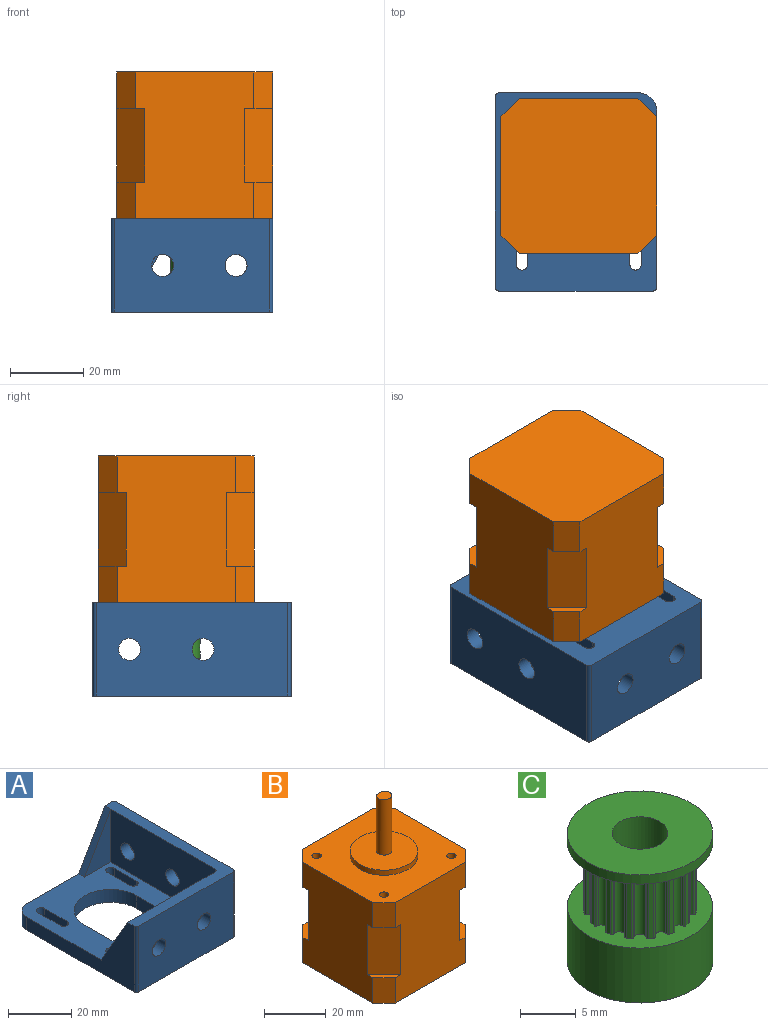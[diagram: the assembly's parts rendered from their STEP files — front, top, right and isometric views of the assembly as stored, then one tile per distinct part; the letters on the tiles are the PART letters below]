
ASSEMBLY  parts=3 mates=4
PART A: 42 faces, bbox 44x54x25.4 mm
  f0: plane 50x40mm, normal (0,0,1), area 1136mm2, adj f1,f2,f3,f4,f5,f6,f7,f8
  f1: cylinder r=1.55mm len=5mm, axis (0,0,-1), area 24.3mm2, adj f0,f2,f24,f25
  f2: plane 10x5mm, normal (-1,0,0), area 50mm2, adj f0,f1,f3,f25
  f3: cylinder r=1.55mm len=5mm, axis (0,0,-1), area 24.3mm2, adj f0,f2,f24,f25
  f4: plane 10x5mm, normal (-1,0,0), area 50mm2, adj f0,f5,f19,f25
  f5: cylinder r=1.55mm len=5mm, axis (0,0,-1), area 24.3mm2, adj f0,f4,f6,f25
  f6: plane 10x5mm, normal (1,0,0), area 50mm2, adj f0,f5,f19,f25
  f7: cylinder r=11.5mm len=23mm, axis (0,0,-1), area 180.6mm2, adj f0,f8,f20,f25
  f8: plane 10x5mm, normal (-1,0,0), area 50mm2, adj f0,f7,f9,f25
  f9: cylinder r=11.5mm len=23mm, axis (0,0,-1), area 180.6mm2, adj f0,f8,f20,f25
  f10: cylinder r=1.55mm len=5mm, axis (0,0,-1), area 24.3mm2, adj f0,f11,f21,f25
  f11: plane 10x5mm, normal (-1,0,0), area 50mm2, adj f0,f10,f12,f25
  f12: cylinder r=1.55mm len=5mm, axis (0,0,-1), area 24.3mm2, adj f0,f11,f21,f25
  f13: cylinder r=1.55mm len=5mm, axis (0,0,-1), area 24.3mm2, adj f0,f14,f22,f25
  f14: plane 10x5mm, normal (-1,0,0), area 50mm2, adj f0,f13,f15,f25
  f15: cylinder r=1.55mm len=5mm, axis (0,0,-1), area 24.3mm2, adj f0,f14,f22,f25
  f16: plane 38x25.4mm, normal (0,1,0), area 371mm2, adj f0,f25,f30,f38,f39,f40
  f17: plane 48x25.4mm, normal (-1,0,0), area 421.1mm2, adj f0,f25,f30,f36,f39,f41
  f18: plane 42x25.4mm, normal (0,-1,0), area 1010.3mm2, adj f25,f30,f31,f32,f36,f37
  f19: cylinder r=1.55mm len=5mm, axis (0,0,-1), area 24.3mm2, adj f0,f4,f6,f25
  f20: plane 10x5mm, normal (1,0,0), area 50mm2, adj f0,f7,f9,f25
  f21: plane 10x5mm, normal (1,0,0), area 50mm2, adj f0,f10,f12,f25
  f22: plane 10x5mm, normal (1,0,0), area 50mm2, adj f0,f13,f15,f25
  f23: plane 52x25.4mm, normal (1,0,0), area 1264.3mm2, adj f25,f30,f33,f34,f37,f38
  f24: plane 10x5mm, normal (1,0,0), area 50mm2, adj f0,f1,f3,f25
  f25: plane 54x44mm, normal (0,0,-1), area 1570.3mm2, adj f1,f2,f3,f4,f5,f6,f7,f8
  f26: plane 20.4x11.75mm, normal (0,-1,0), area 119.8mm2, adj f0,f27,f40
  f27: plane 46.5x20.4mm, normal (-1,0,0), area 892.1mm2, adj f0,f26,f30,f33,f34,f35
  f28: plane 36.5x20.4mm, normal (0,1,0), area 688.1mm2, adj f0,f29,f30,f31,f32,f35
  f29: plane 20.4x11.75mm, normal (1,0,0), area 119.9mm2, adj f0,f28,f41
  f30: plane 54x44mm, normal (0,0,1), area 375.6mm2, adj f16,f17,f18,f23,f27,f28,f35,f36
  f31: cylinder r=3mm len=6mm, axis (0,1,0), area 75.4mm2, adj f18,f28
  f32: cylinder r=3mm len=6mm, axis (0,1,0), area 75.4mm2, adj f18,f28
  f33: cylinder r=3mm len=6mm, axis (-1,0,0), area 75.4mm2, adj f23,f27
  f34: cylinder r=3mm len=6mm, axis (-1,0,0), area 75.4mm2, adj f23,f27
  f35: cylinder r=1mm len=20.4mm, axis (0,0,1), area 32mm2, adj f0,f27,f28,f30
  f36: cylinder r=1mm len=25.4mm, axis (0,0,-1), area 39.9mm2, adj f17,f18,f25,f30
  f37: cylinder r=1mm len=25.4mm, axis (0,0,-1), area 39.9mm2, adj f18,f23,f25,f30
  f38: cylinder r=1mm len=25.4mm, axis (0,0,1), area 39.9mm2, adj f16,f23,f25,f30
  f39: cylinder r=5mm len=5mm, axis (0,0,1), area 39.3mm2, adj f0,f16,f17,f25
  f40: plane 20.4x11.75mm, normal (-0.87,0,0.5), area 58.9mm2, adj f0,f16,f26,f30
  f41: plane 20.4x11.75mm, normal (0,0.87,0.5), area 58.9mm2, adj f0,f17,f29,f30
PART B: 40 faces, bbox 42.4x42.4x64 mm
  f0: plane 40x32.26mm, normal (-1,0,0), area 1188.7mm2, adj f5,f6,f10,f11,f12,f14,f15,f18
  f1: plane 40x32.26mm, normal (0,-1,0), area 1188.7mm2, adj f4,f5,f8,f11,f12,f13,f14,f17
  f2: plane 40x32.26mm, normal (1,0,0), area 1188.7mm2, adj f4,f7,f8,f9,f12,f13,f16,f17
  f3: plane 40x32.26mm, normal (0,1,0), area 1188.7mm2, adj f6,f7,f9,f10,f12,f15,f16,f19
  f4: plane 20x7.62mm, normal (0.71,-0.71,0), area 215.5mm2, adj f1,f2,f8,f17
  f5: plane 20x7.62mm, normal (-0.71,-0.71,0), area 215.5mm2, adj f0,f1,f11,f18
  f6: plane 20x7.62mm, normal (-0.71,0.71,0), area 215.5mm2, adj f0,f3,f10,f19
  f7: plane 20x7.62mm, normal (0.71,0.71,0), area 215.5mm2, adj f2,f3,f9,f20
  f8: plane 7.62x7.62mm, normal (0,0,-1), area 16.1mm2, adj f1,f2,f4,f13
  f9: plane 7.62x7.62mm, normal (0,0,-1), area 16.1mm2, adj f2,f3,f7,f16
  f10: plane 7.62x7.62mm, normal (0,0,-1), area 16.1mm2, adj f0,f3,f6,f15
  f11: plane 7.62x7.62mm, normal (0,0,-1), area 16.1mm2, adj f0,f1,f5,f14
  f12: plane 42.42x42.42mm, normal (0,0,1), area 1339.4mm2, adj f0,f1,f2,f3,f13,f14,f15,f16
  f13: plane 10x5.08mm, normal (0.71,-0.71,0), area 71.8mm2, adj f1,f2,f8,f12
  f14: plane 10x5.08mm, normal (-0.71,-0.71,0), area 71.8mm2, adj f0,f1,f11,f12
  f15: plane 10x5.08mm, normal (-0.71,0.71,0), area 71.8mm2, adj f0,f3,f10,f12
  f16: plane 10x5.08mm, normal (0.71,0.71,0), area 71.8mm2, adj f2,f3,f9,f12
  f17: plane 7.62x7.62mm, normal (0,0,1), area 16.1mm2, adj f1,f2,f4,f23
  f18: plane 7.62x7.62mm, normal (0,0,1), area 16.1mm2, adj f0,f1,f5,f24
  f19: plane 7.62x7.62mm, normal (0,0,1), area 16.1mm2, adj f0,f3,f6,f21
  f20: plane 7.62x7.62mm, normal (0,0,1), area 16.1mm2, adj f2,f3,f7,f22
  f21: plane 10x5.08mm, normal (-0.71,0.71,0), area 71.8mm2, adj f0,f3,f19,f25
  f22: plane 10x5.08mm, normal (0.71,0.71,0), area 71.8mm2, adj f2,f3,f20,f25
  f23: plane 10x5.08mm, normal (0.71,-0.71,0), area 71.8mm2, adj f1,f2,f17,f25
  f24: plane 10x5.08mm, normal (-0.71,-0.71,0), area 71.8mm2, adj f0,f1,f18,f25
  f25: plane 42.42x42.42mm, normal (0,0,-1), area 1747.7mm2, adj f0,f1,f2,f3,f21,f22,f23,f24
  f26: cylinder r=11mm len=22mm, axis (0,0,-1), area 138.2mm2, adj f12,f27
  f27: plane 22x22mm, normal (0,0,1), area 360.4mm2, adj f26,f28
  f28: cylinder r=2.5mm len=22mm, axis (0,0,-1), area 297.3mm2, adj f27,f29,f30,f31
  f29: plane 5x4.5mm, normal (0,0,1), area 18.6mm2, adj f28,f31
  f30: plane 3x0.5mm, normal (0,0,1), area 1mm2, adj f28,f31
  f31: plane 15x3mm, normal (0,1,0), area 45mm2, adj f28,f29,f30
  f32: cylinder r=1.5mm len=6.35mm, axis (0,0,1), area 59.8mm2, adj f12,f33
  f33: plane 3x3mm, normal (0,0,1), area 7.1mm2, adj f32
  f34: cylinder r=1.5mm len=6.35mm, axis (0,0,1), area 59.8mm2, adj f12,f35
  f35: plane 3x3mm, normal (0,0,1), area 7.1mm2, adj f34
  f36: cylinder r=1.5mm len=6.35mm, axis (0,0,1), area 59.8mm2, adj f12,f37
  f37: plane 3x3mm, normal (0,0,1), area 7.1mm2, adj f36
  f38: cylinder r=1.5mm len=6.35mm, axis (0,0,1), area 59.8mm2, adj f12,f39
  f39: plane 3x3mm, normal (0,0,1), area 7.1mm2, adj f38
PART C: 104 faces, bbox 13x13x14 mm
  f0: cylinder r=2.5mm len=14mm, axis (0,0,1), area 214.8mm2, adj f2,f102,f103
  f1: cylinder r=6.5mm len=13mm, axis (0,0,1), area 240.1mm2, adj f2,f3,f103
  f2: plane 13x13mm, normal (0,0,-1), area 113.1mm2, adj f0,f1
  f3: plane 13x13mm, normal (0,0,1), area 62.7mm2, adj f1,f4,f5,f6,f7,f8,f9,f10
  f4: cylinder r=0.15mm len=7mm, axis (0,0,-1), area 1.7mm2, adj f3,f5,f99,f100
  f5: cylinder r=1mm len=7mm, axis (0,0,-1), area 1.7mm2, adj f3,f4,f6,f100
  f6: cylinder r=0.56mm len=7mm, axis (0,0,-1), area 9mm2, adj f3,f5,f7,f100
  f7: cylinder r=1mm len=7mm, axis (0,0,-1), area 1.7mm2, adj f3,f6,f8,f100
  f8: cylinder r=0.15mm len=7mm, axis (0,0,-1), area 1.7mm2, adj f3,f7,f9,f100
  f9: plane 7x0.49mm, normal (0.98,0.2,0), area 3.5mm2, adj f3,f8,f10,f100
  f10: cylinder r=0.15mm len=7mm, axis (0,0,-1), area 1.7mm2, adj f3,f9,f11,f100
  f11: cylinder r=1mm len=7mm, axis (0,0,-1), area 1.7mm2, adj f3,f10,f12,f100
  f12: cylinder r=0.56mm len=7mm, axis (0,0,-1), area 9mm2, adj f3,f11,f13,f100
  f13: cylinder r=1mm len=7mm, axis (0,0,-1), area 1.7mm2, adj f3,f12,f14,f100
  f14: cylinder r=0.15mm len=7mm, axis (0,0,-1), area 1.7mm2, adj f3,f13,f15,f100
  f15: plane 7x0.41mm, normal (0.83,0.56,0), area 3.5mm2, adj f3,f14,f16,f100
  f16: cylinder r=0.15mm len=7mm, axis (0,0,-1), area 1.7mm2, adj f3,f15,f17,f100
  f17: cylinder r=1mm len=7mm, axis (0,0,-1), area 1.7mm2, adj f3,f16,f18,f100
  f18: cylinder r=0.56mm len=7mm, axis (0,0,-1), area 9mm2, adj f3,f17,f19,f100
  f19: cylinder r=1mm len=7mm, axis (0,0,-1), area 1.7mm2, adj f3,f18,f20,f100
  f20: cylinder r=0.15mm len=7mm, axis (0,0,-1), area 1.7mm2, adj f3,f19,f21,f100
  f21: plane 7x0.41mm, normal (0.56,0.83,0), area 3.5mm2, adj f3,f20,f22,f100
  f22: cylinder r=0.15mm len=7mm, axis (0,0,-1), area 1.7mm2, adj f3,f21,f23,f100
  f23: cylinder r=1mm len=7mm, axis (0,0,-1), area 1.7mm2, adj f3,f22,f24,f100
  f24: cylinder r=0.56mm len=7mm, axis (0,0,-1), area 9mm2, adj f3,f23,f25,f100
  f25: cylinder r=1mm len=7mm, axis (0,0,-1), area 1.7mm2, adj f3,f24,f26,f100
  f26: cylinder r=0.15mm len=7mm, axis (0,0,-1), area 1.7mm2, adj f3,f25,f27,f100
  f27: plane 7x0.49mm, normal (0.2,0.98,0), area 3.5mm2, adj f3,f26,f28,f100
  f28: cylinder r=0.15mm len=7mm, axis (0,0,-1), area 1.7mm2, adj f3,f27,f29,f100
  f29: cylinder r=1mm len=7mm, axis (0,0,-1), area 1.7mm2, adj f3,f28,f30,f100
  f30: cylinder r=0.56mm len=7mm, axis (0,0,-1), area 9mm2, adj f3,f29,f31,f100
  f31: cylinder r=1mm len=7mm, axis (0,0,-1), area 1.7mm2, adj f3,f30,f32,f100
  f32: cylinder r=0.15mm len=7mm, axis (0,0,-1), area 1.7mm2, adj f3,f31,f33,f100
  f33: plane 7x0.49mm, normal (-0.2,0.98,0), area 3.5mm2, adj f3,f32,f34,f100
  f34: cylinder r=0.15mm len=7mm, axis (0,0,-1), area 1.7mm2, adj f3,f33,f35,f100
  f35: cylinder r=1mm len=7mm, axis (0,0,-1), area 1.7mm2, adj f3,f34,f36,f100
  f36: cylinder r=0.56mm len=7mm, axis (0,0,-1), area 9mm2, adj f3,f35,f37,f100
  f37: cylinder r=1mm len=7mm, axis (0,0,-1), area 1.7mm2, adj f3,f36,f38,f100
  f38: cylinder r=0.15mm len=7mm, axis (0,0,-1), area 1.7mm2, adj f3,f37,f39,f100
  f39: plane 7x0.41mm, normal (-0.56,0.83,0), area 3.5mm2, adj f3,f38,f40,f100
  f40: cylinder r=0.15mm len=7mm, axis (0,0,-1), area 1.7mm2, adj f3,f39,f41,f100
  f41: cylinder r=1mm len=7mm, axis (0,0,-1), area 1.7mm2, adj f3,f40,f42,f100
  f42: cylinder r=0.56mm len=7mm, axis (0,0,-1), area 9mm2, adj f3,f41,f43,f100
  f43: cylinder r=1mm len=7mm, axis (0,0,-1), area 1.7mm2, adj f3,f42,f44,f100
  f44: cylinder r=0.15mm len=7mm, axis (0,0,-1), area 1.7mm2, adj f3,f43,f45,f100
  f45: plane 7x0.41mm, normal (-0.83,0.56,0), area 3.5mm2, adj f3,f44,f46,f100
  f46: cylinder r=0.15mm len=7mm, axis (0,0,-1), area 1.7mm2, adj f3,f45,f47,f100
  f47: cylinder r=1mm len=7mm, axis (0,0,-1), area 1.7mm2, adj f3,f46,f48,f100
  f48: cylinder r=0.56mm len=7mm, axis (0,0,-1), area 9mm2, adj f3,f47,f49,f100
  f49: cylinder r=1mm len=7mm, axis (0,0,-1), area 1.7mm2, adj f3,f48,f50,f100
  f50: cylinder r=0.15mm len=7mm, axis (0,0,-1), area 1.7mm2, adj f3,f49,f51,f100
  f51: plane 7x0.49mm, normal (-0.98,0.2,0), area 3.5mm2, adj f3,f50,f52,f100
  f52: cylinder r=0.15mm len=7mm, axis (0,0,-1), area 1.7mm2, adj f3,f51,f53,f100
  f53: cylinder r=1mm len=7mm, axis (0,0,-1), area 1.7mm2, adj f3,f52,f54,f100
  f54: cylinder r=0.56mm len=7mm, axis (0,0,-1), area 9mm2, adj f3,f53,f55,f100
  f55: cylinder r=1mm len=7mm, axis (0,0,-1), area 1.7mm2, adj f3,f54,f56,f100
  f56: cylinder r=0.15mm len=7mm, axis (0,0,-1), area 1.7mm2, adj f3,f55,f57,f100
  f57: plane 7x0.49mm, normal (-0.98,-0.2,0), area 3.5mm2, adj f3,f56,f58,f100
  f58: cylinder r=0.15mm len=7mm, axis (0,0,-1), area 1.7mm2, adj f3,f57,f59,f100
  f59: cylinder r=1mm len=7mm, axis (0,0,-1), area 1.7mm2, adj f3,f58,f60,f100
  f60: cylinder r=0.56mm len=7mm, axis (0,0,-1), area 9mm2, adj f3,f59,f61,f100
  f61: cylinder r=1mm len=7mm, axis (0,0,-1), area 1.7mm2, adj f3,f60,f62,f100
  f62: cylinder r=0.15mm len=7mm, axis (0,0,-1), area 1.7mm2, adj f3,f61,f63,f100
  f63: plane 7x0.41mm, normal (-0.83,-0.56,0), area 3.5mm2, adj f3,f62,f64,f100
  f64: cylinder r=0.15mm len=7mm, axis (0,0,-1), area 1.7mm2, adj f3,f63,f65,f100
  f65: cylinder r=1mm len=7mm, axis (0,0,-1), area 1.7mm2, adj f3,f64,f66,f100
  f66: cylinder r=0.56mm len=7mm, axis (0,0,-1), area 9mm2, adj f3,f65,f67,f100
  f67: cylinder r=1mm len=7mm, axis (0,0,-1), area 1.7mm2, adj f3,f66,f68,f100
  f68: cylinder r=0.15mm len=7mm, axis (0,0,-1), area 1.7mm2, adj f3,f67,f69,f100
  f69: plane 7x0.41mm, normal (-0.56,-0.83,0), area 3.5mm2, adj f3,f68,f70,f100
  f70: cylinder r=0.15mm len=7mm, axis (0,0,-1), area 1.7mm2, adj f3,f69,f71,f100
  f71: cylinder r=1mm len=7mm, axis (0,0,-1), area 1.7mm2, adj f3,f70,f72,f100
  f72: cylinder r=0.56mm len=7mm, axis (0,0,-1), area 9mm2, adj f3,f71,f73,f100
  f73: cylinder r=1mm len=7mm, axis (0,0,-1), area 1.7mm2, adj f3,f72,f74,f100
  f74: cylinder r=0.15mm len=7mm, axis (0,0,-1), area 1.7mm2, adj f3,f73,f75,f100
  f75: plane 7x0.49mm, normal (-0.2,-0.98,0), area 3.5mm2, adj f3,f74,f76,f100
  f76: cylinder r=0.15mm len=7mm, axis (0,0,-1), area 1.7mm2, adj f3,f75,f77,f100
  f77: cylinder r=1mm len=7mm, axis (0,0,-1), area 1.7mm2, adj f3,f76,f78,f100
  f78: cylinder r=0.56mm len=7mm, axis (0,0,-1), area 9mm2, adj f3,f77,f79,f100
  f79: cylinder r=1mm len=7mm, axis (0,0,-1), area 1.7mm2, adj f3,f78,f80,f100
  f80: cylinder r=0.15mm len=7mm, axis (0,0,-1), area 1.7mm2, adj f3,f79,f81,f100
  f81: plane 7x0.49mm, normal (0.2,-0.98,0), area 3.5mm2, adj f3,f80,f82,f100
  f82: cylinder r=0.15mm len=7mm, axis (0,0,-1), area 1.7mm2, adj f3,f81,f83,f100
  f83: cylinder r=1mm len=7mm, axis (0,0,-1), area 1.7mm2, adj f3,f82,f84,f100
  f84: cylinder r=0.56mm len=7mm, axis (0,0,-1), area 9mm2, adj f3,f83,f85,f100
  f85: cylinder r=1mm len=7mm, axis (0,0,-1), area 1.7mm2, adj f3,f84,f86,f100
  f86: cylinder r=0.15mm len=7mm, axis (0,0,-1), area 1.7mm2, adj f3,f85,f87,f100
  f87: plane 7x0.41mm, normal (0.56,-0.83,0), area 3.5mm2, adj f3,f86,f88,f100
  f88: cylinder r=0.15mm len=7mm, axis (0,0,-1), area 1.7mm2, adj f3,f87,f89,f100
  f89: cylinder r=1mm len=7mm, axis (0,0,-1), area 1.7mm2, adj f3,f88,f90,f100
  f90: cylinder r=0.56mm len=7mm, axis (0,0,-1), area 9mm2, adj f3,f89,f91,f100
  f91: cylinder r=1mm len=7mm, axis (0,0,-1), area 1.7mm2, adj f3,f90,f92,f100
  f92: cylinder r=0.15mm len=7mm, axis (0,0,-1), area 1.7mm2, adj f3,f91,f93,f100
  f93: plane 7x0.41mm, normal (0.83,-0.56,0), area 3.5mm2, adj f3,f92,f94,f100
  f94: cylinder r=0.15mm len=7mm, axis (0,0,-1), area 1.7mm2, adj f3,f93,f95,f100
  f95: cylinder r=1mm len=7mm, axis (0,0,-1), area 1.7mm2, adj f3,f94,f96,f100
  f96: cylinder r=0.56mm len=7mm, axis (0,0,-1), area 9mm2, adj f3,f95,f97,f100
  f97: cylinder r=1mm len=7mm, axis (0,0,-1), area 1.7mm2, adj f3,f96,f98,f100
  f98: cylinder r=0.15mm len=7mm, axis (0,0,-1), area 1.7mm2, adj f3,f97,f99,f100
  f99: plane 7x0.49mm, normal (0.98,-0.2,0), area 3.5mm2, adj f3,f4,f98,f100
  f100: plane 13x13mm, normal (0,0,-1), area 62.7mm2, adj f4,f5,f6,f7,f8,f9,f10,f11
  f101: cylinder r=6.5mm len=13mm, axis (0,0,-1), area 40.8mm2, adj f100,f102
  f102: plane 13x13mm, normal (0,0,1), area 113.1mm2, adj f0,f101
  f103: cylinder r=1.25mm len=4.34mm, axis (0,-1,0), area 32.2mm2, adj f0,f1
PLACE A rot(axis=(0,1,0),180deg) t=(-6.51,-59.85,26.7)mm
PLACE B rot(axis=(0,1,0),180deg) t=(-6.51,-51.31,46.7)mm
PLACE C rot(axis=(1,0,0),180deg) t=(-6.51,-51.31,11.58)mm
MATE pin_slot B.f32 <-> A.f1  axis (0,0,-1) through (-22.01,-35.81,26.7)mm
MATE planar A.f25 <-> B.f26  axis (0,0,1) through (-7.71,-56.07,26.7)mm
MATE cylindrical C.f0 <-> B.f26  axis (0,0,-1) through (-6.51,-51.31,10.58)mm
MATE pin_slot B.f38 <-> A.f13  axis (0,0,-1) through (8.99,-35.81,26.7)mm
